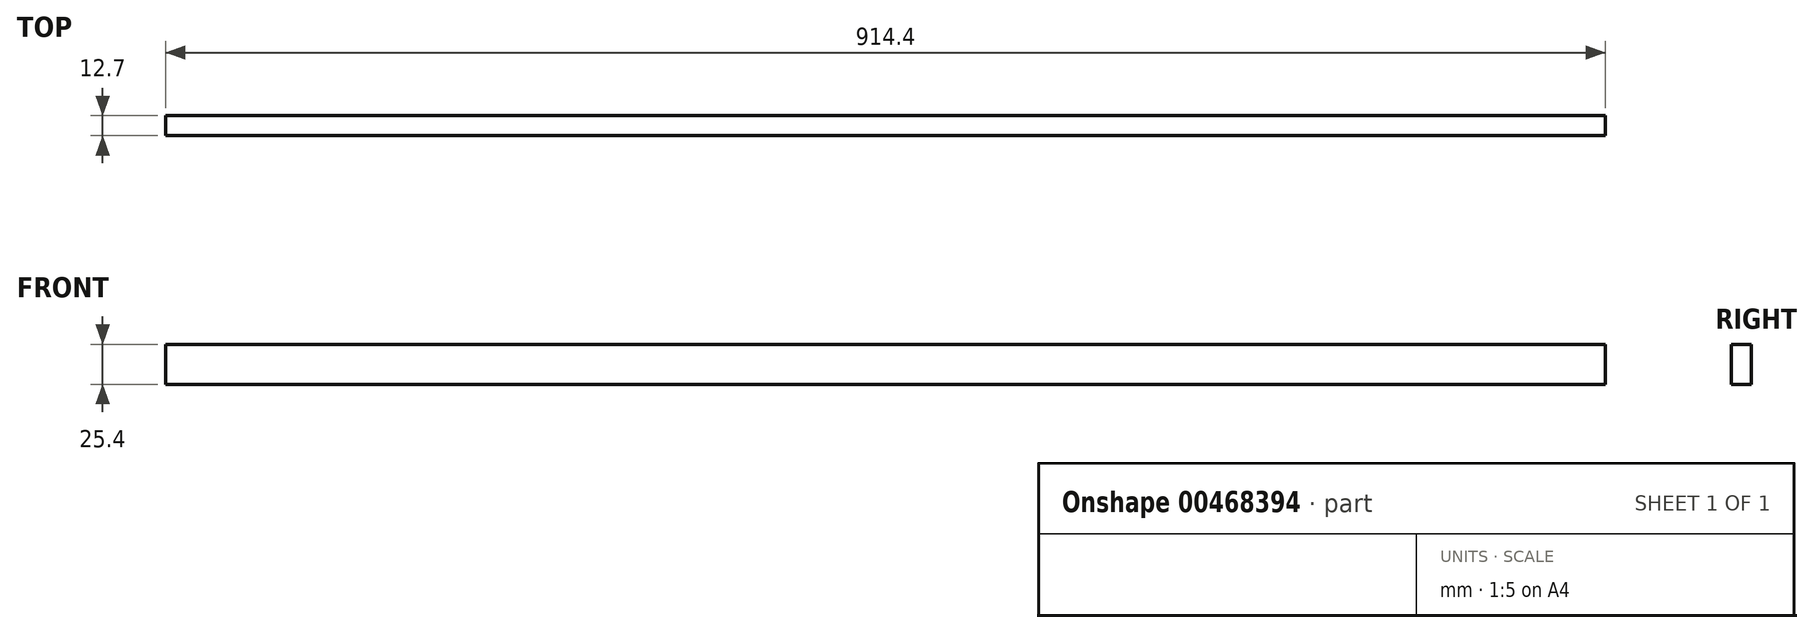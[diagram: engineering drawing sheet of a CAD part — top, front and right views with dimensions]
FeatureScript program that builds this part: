
annotation { "Feature Type Name" : "Feature", "Feature Type Description" : "" }
export const myFeature = defineFeature(function(context is Context, id is Id, definition is map)
    precondition{}
    {
        {
            var Q0;
            Q0=qCreatedBy(makeId("Front.planeOp"),FACE);
            var sketch = newSketch(context, id + "F0", { "sketchPlane" : qUnion([Q0])});
            skLineSegment(sketch, "E0.bottom", {"start": v(457.2, -12.7) * mm, "end": v(-457.2, -12.7) * mm});
            skLineSegment(sketch, "E0.top", {"start": v(457.2, 12.7) * mm, "end": v(-457.2, 12.7) * mm});
            skLineSegment(sketch, "E0.left", {"start": v(457.2, -12.7) * mm, "end": v(457.2, 12.7) * mm});
            skLineSegment(sketch, "E0.right", {"start": v(-457.2, -12.7) * mm, "end": v(-457.2, 12.7) * mm});
            skPoint(sketch, "E0.middle", {"position": v(0, 0) * mm});
            skSolve(sketch);
        }
        {
            var Q0;
            Q0=makeQuery(id+"F0.imprint","IMPRINT",FACE,{"disambiguationData":[TD([[makeQuery(id+"F0.imprint","IMPRINT",EDGE,{"derivedFrom":sQuery(id+"F0.wireOp",EDGE,"E0.bottom")}),-1.0]])]});
            extrude(context, id + "F1", {"entities" : qUnion([Q0]), "endBound" : BoundingType.SYMMETRIC, "depth" : 12.7 * mm});
        }
    });
